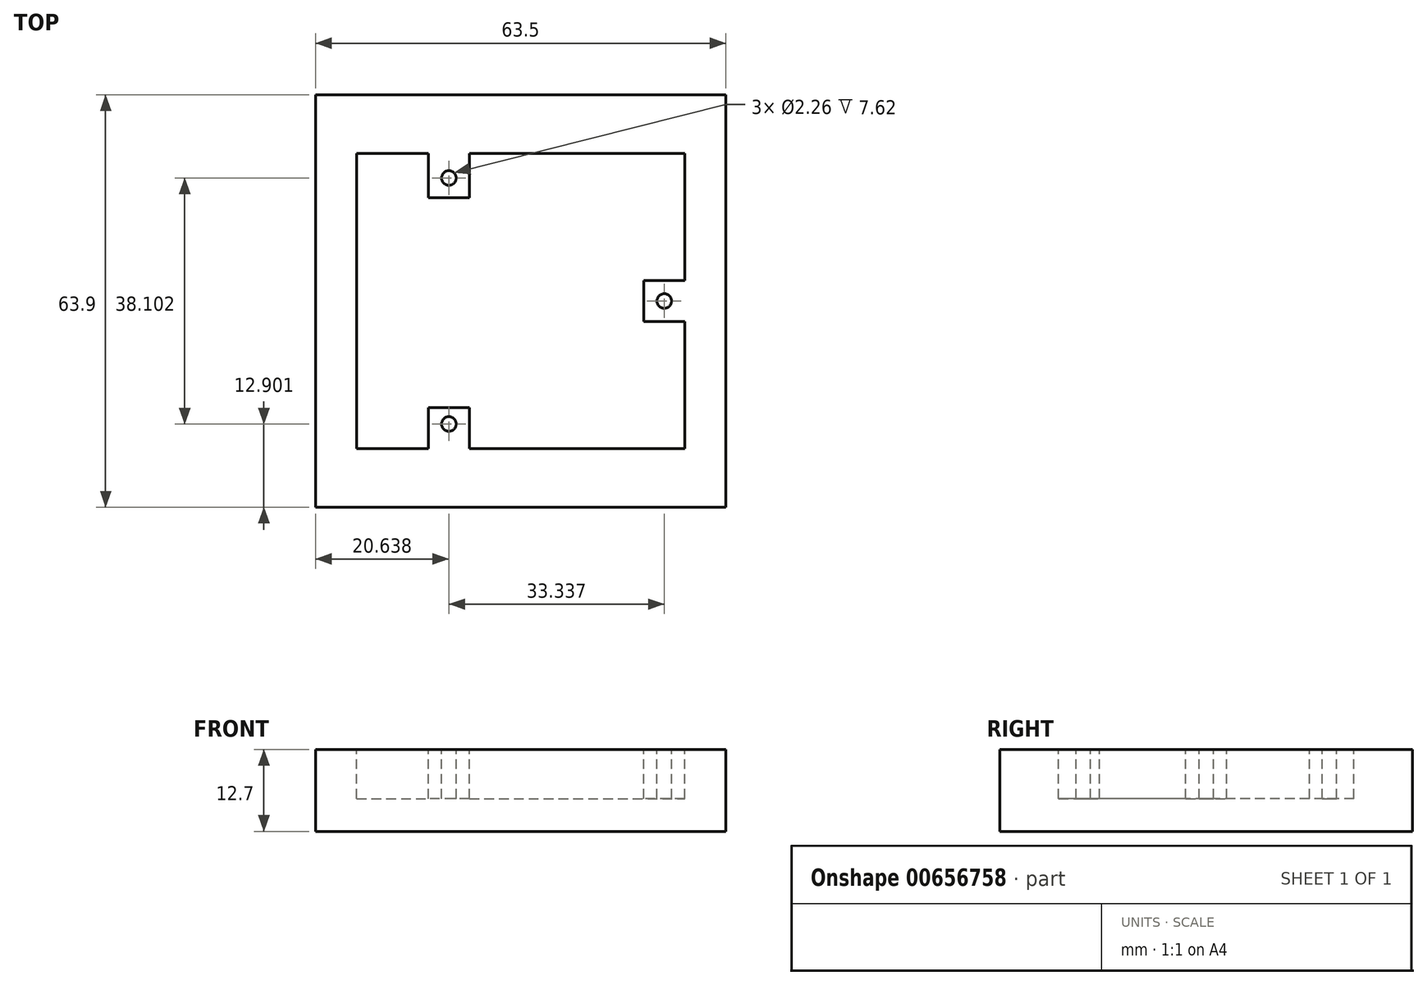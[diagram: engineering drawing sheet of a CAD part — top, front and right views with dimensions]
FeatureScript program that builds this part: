
annotation { "Feature Type Name" : "Feature", "Feature Type Description" : "" }
export const myFeature = defineFeature(function(context is Context, id is Id, definition is map)
    precondition{}
    {
        {
            var Q0;
            Q0=qCreatedBy(makeId("Top.planeOp"),FACE);
            var sketch = newSketch(context, id + "F0", { "sketchPlane" : qUnion([Q0])});
            skLineSegment(sketch, "E0.bottom", {"start": v(-25.4, 25.4) * mm, "end": v(25.4, 25.4) * mm});
            skLineSegment(sketch, "E0.top", {"start": v(-25.4, -25.4) * mm, "end": v(25.4, -25.4) * mm});
            skLineSegment(sketch, "E0.left", {"start": v(-25.4, 25.4) * mm, "end": v(-25.4, -25.4) * mm});
            skLineSegment(sketch, "E0.right", {"start": v(25.4, 25.4) * mm, "end": v(25.4, -25.4) * mm});
            skLineSegment(sketch, "E1", {"start": v(0, 25.4) * mm, "end": v(0, 0) * mm, "construction": true});
            skLineSegment(sketch, "E2", {"start": v(0, 0) * mm, "end": v(0, -25.4) * mm, "construction": true});
            skCircle(sketch, "E3", {"center": v(-11.11, 19.05) * mm, "radius": 1.73 * mm});
            skLineSegment(sketch, "E4", {"start": v(-11.11, 19.05) * mm, "end": v(-11.11, 25.4) * mm});
            skLineSegment(sketch, "E5", {"start": v(-11.11, 25.4) * mm, "end": v(-11.11, 19.05) * mm});
            skLineSegment(sketch, "E6", {"start": v(-25.4, 19.05) * mm, "end": v(-11.11, 19.05) * mm, "construction": true});
            skCircle(sketch, "E7", {"center": v(-11.11, -19.05) * mm, "radius": 1.73 * mm});
            skCircle(sketch, "E8", {"center": v(22.22, 0) * mm, "radius": 1.73 * mm});
            skLineSegment(sketch, "E9", {"start": v(-11.11, -19.05) * mm, "end": v(-25.4, -19.05) * mm, "construction": true});
            skLineSegment(sketch, "E10", {"start": v(-11.11, -19.05) * mm, "end": v(-11.11, -25.4) * mm, "construction": true});
            skLineSegment(sketch, "E11", {"start": v(22.22, 0) * mm, "end": v(22.22, 25.4) * mm, "construction": true});
            skLineSegment(sketch, "E12", {"start": v(22.22, 0) * mm, "end": v(25.4, 0) * mm, "construction": true});
            skSolve(sketch);
        }
        {
            var Q0;
            Q0=qCreatedBy(makeId("Top.planeOp"),FACE);
            var sketch = newSketch(context, id + "F1", { "sketchPlane" : qUnion([Q0])});
            skLineSegment(sketch, "E13.bottom", {"start": v(-31.75, 31.95) * mm, "end": v(31.75, 31.95) * mm});
            skLineSegment(sketch, "E13.top", {"start": v(-31.75, -31.95) * mm, "end": v(31.75, -31.95) * mm});
            skLineSegment(sketch, "E13.left", {"start": v(-31.75, 31.95) * mm, "end": v(-31.75, -31.95) * mm});
            skLineSegment(sketch, "E13.right", {"start": v(31.75, 31.95) * mm, "end": v(31.75, -31.95) * mm});
            skSolve(sketch);
        }
        {
            var Q0;
            Q0=qCreatedBy(makeId("Top.planeOp"),FACE);
            var sketch = newSketch(context, id + "F2", { "sketchPlane" : qUnion([Q0])});
            skLineSegment(sketch, "E14.bottom", {"start": v(-25.4, 22.86) * mm, "end": v(-14.29, 22.86) * mm});
            skLineSegment(sketch, "E14.top", {"start": v(-25.4, -22.86) * mm, "end": v(-14.29, -22.86) * mm});
            skLineSegment(sketch, "E14.left", {"start": v(-25.4, 22.86) * mm, "end": v(-25.4, -22.86) * mm});
            skLineSegment(sketch, "E14.right", {"start": v(25.4, 22.86) * mm, "end": v(25.4, 3.17) * mm});
            skLineSegment(sketch, "E15.top", {"start": v(-14.29, 16) * mm, "end": v(-7.94, 16) * mm});
            skLineSegment(sketch, "E15.left", {"start": v(-14.29, 22.86) * mm, "end": v(-14.29, 16) * mm});
            skLineSegment(sketch, "E15.right", {"start": v(-7.94, 22.86) * mm, "end": v(-7.94, 16) * mm});
            skPoint(sketch, "E16", {"position": v(-14.29, 22.86) * mm});
            skPoint(sketch, "E17", {"position": v(-7.94, 22.86) * mm});
            skLineSegment(sketch, "E18.trimOffspring", {"start": v(-7.94, 22.86) * mm, "end": v(25.4, 22.86) * mm});
            skLineSegment(sketch, "E19.top", {"start": v(-7.94, -16.51) * mm, "end": v(-14.29, -16.51) * mm});
            skLineSegment(sketch, "E19.left", {"start": v(-7.94, -22.86) * mm, "end": v(-7.94, -16.51) * mm});
            skLineSegment(sketch, "E19.right", {"start": v(-14.29, -22.86) * mm, "end": v(-14.29, -16.51) * mm});
            skPoint(sketch, "E19.middle", {"position": v(-11.11, -19.69) * mm});
            skLineSegment(sketch, "E20.trimOffspring", {"start": v(-7.94, -22.86) * mm, "end": v(25.4, -22.86) * mm});
            skLineSegment(sketch, "E21.bottom", {"start": v(25.4, -3.18) * mm, "end": v(19.05, -3.18) * mm});
            skLineSegment(sketch, "E21.top", {"start": v(25.4, 3.17) * mm, "end": v(19.05, 3.17) * mm});
            skLineSegment(sketch, "E21.right", {"start": v(19.05, -3.18) * mm, "end": v(19.05, 3.17) * mm});
            skPoint(sketch, "E21.middle", {"position": v(22.23, 0) * mm});
            skLineSegment(sketch, "E22.trimOffspring", {"start": v(25.4, -3.18) * mm, "end": v(25.4, -22.86) * mm});
            skCircle(sketch, "E23", {"center": v(22.23, 0) * mm, "radius": 1.13 * mm});
            skCircle(sketch, "E24", {"center": v(-11.11, -19.05) * mm, "radius": 1.13 * mm});
            skCircle(sketch, "E25", {"center": v(-11.11, 19.05) * mm, "radius": 1.13 * mm});
            skSolve(sketch);
        }
        {
            var Q0;
            Q0 = qSketchRegion(id + "F1", true);
            extrude(context, id + "F3", {"entities" : qUnion([Q0]), "depth" : -12.7 * mm, "offsetDistance" : 25.4 * mm});
        }
        {
            var Q0;
            Q0 = qSketchRegion(id + "F2", true);
            extrude(context, id + "F4", {"entities" : qUnion([Q0]), "operationType" : NewBodyOperationType.REMOVE, "depth" : -7.62 * mm, "offsetDistance" : 25.4 * mm});
        }
    });
